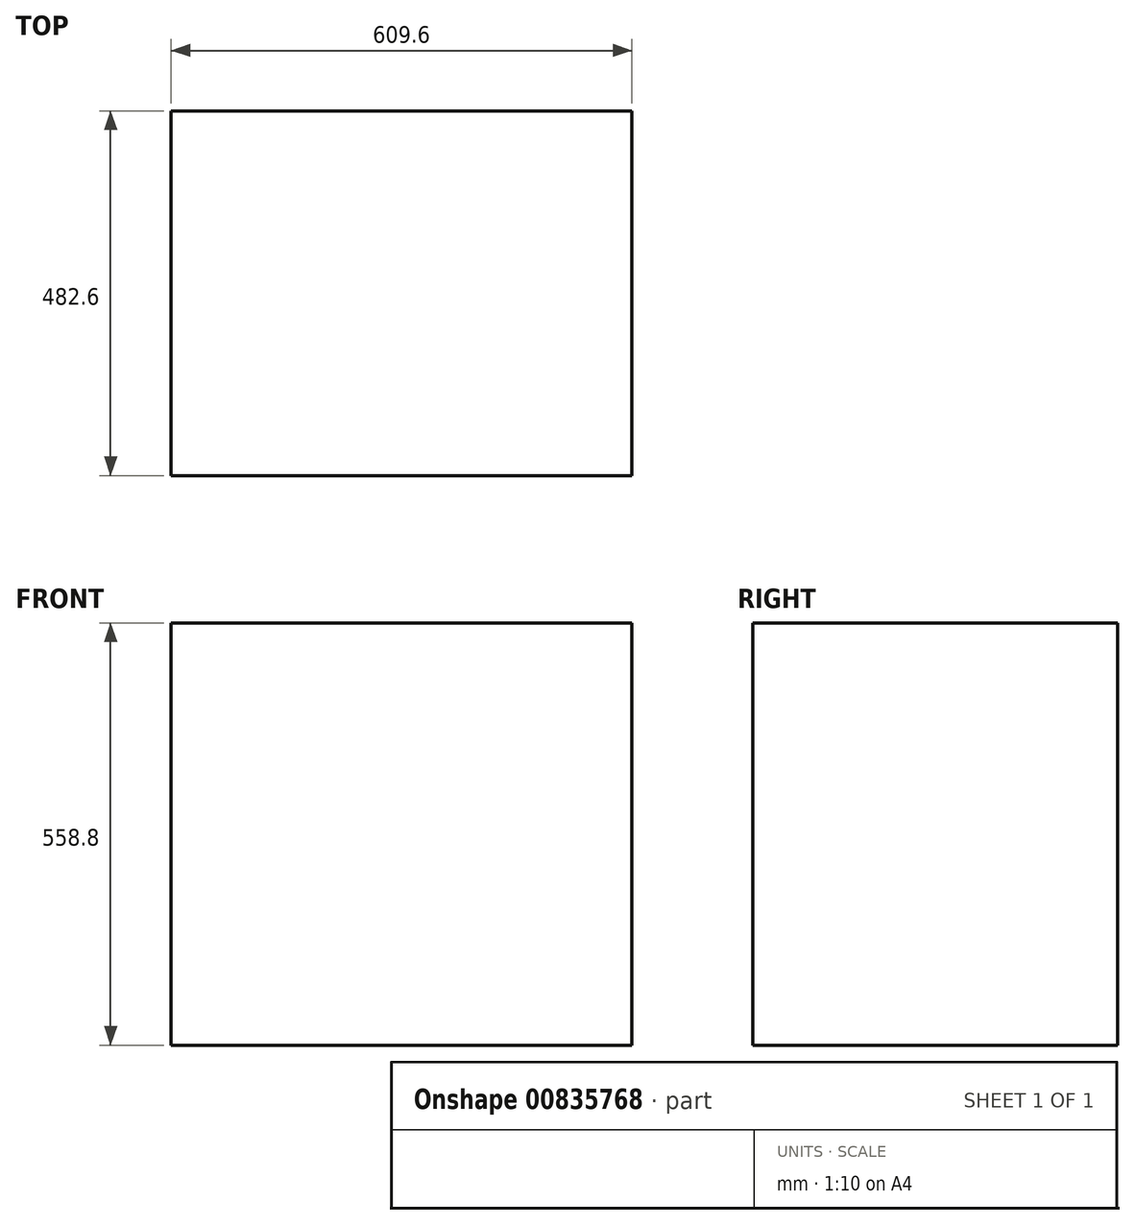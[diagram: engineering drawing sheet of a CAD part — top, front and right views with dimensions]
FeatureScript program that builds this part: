
annotation { "Feature Type Name" : "Feature", "Feature Type Description" : "" }
export const myFeature = defineFeature(function(context is Context, id is Id, definition is map)
    precondition{}
    {
        {
            var Q0;
            Q0=qCreatedBy(makeId("Top.planeOp"),FACE);
            var sketch = newSketch(context, id + "F0", { "sketchPlane" : qUnion([Q0])});
            skLineSegment(sketch, "E0.bottom", {"start": v(304.8, 241.3) * mm, "end": v(-304.8, 241.3) * mm});
            skLineSegment(sketch, "E0.top", {"start": v(304.8, -241.3) * mm, "end": v(-304.8, -241.3) * mm});
            skLineSegment(sketch, "E0.left", {"start": v(304.8, 241.3) * mm, "end": v(304.8, -241.3) * mm});
            skLineSegment(sketch, "E0.right", {"start": v(-304.8, 241.3) * mm, "end": v(-304.8, -241.3) * mm});
            skPoint(sketch, "E0.middle", {"position": v(0, 0) * mm});
            skSolve(sketch);
        }
        {
            var Q0;
            Q0 = qSketchRegion(id + "F0", true);
            extrude(context, id + "F1", {"entities" : qUnion([Q0]), "depth" : 558.8 * mm, "offsetDistance" : 25.4 * mm});
        }
    });
